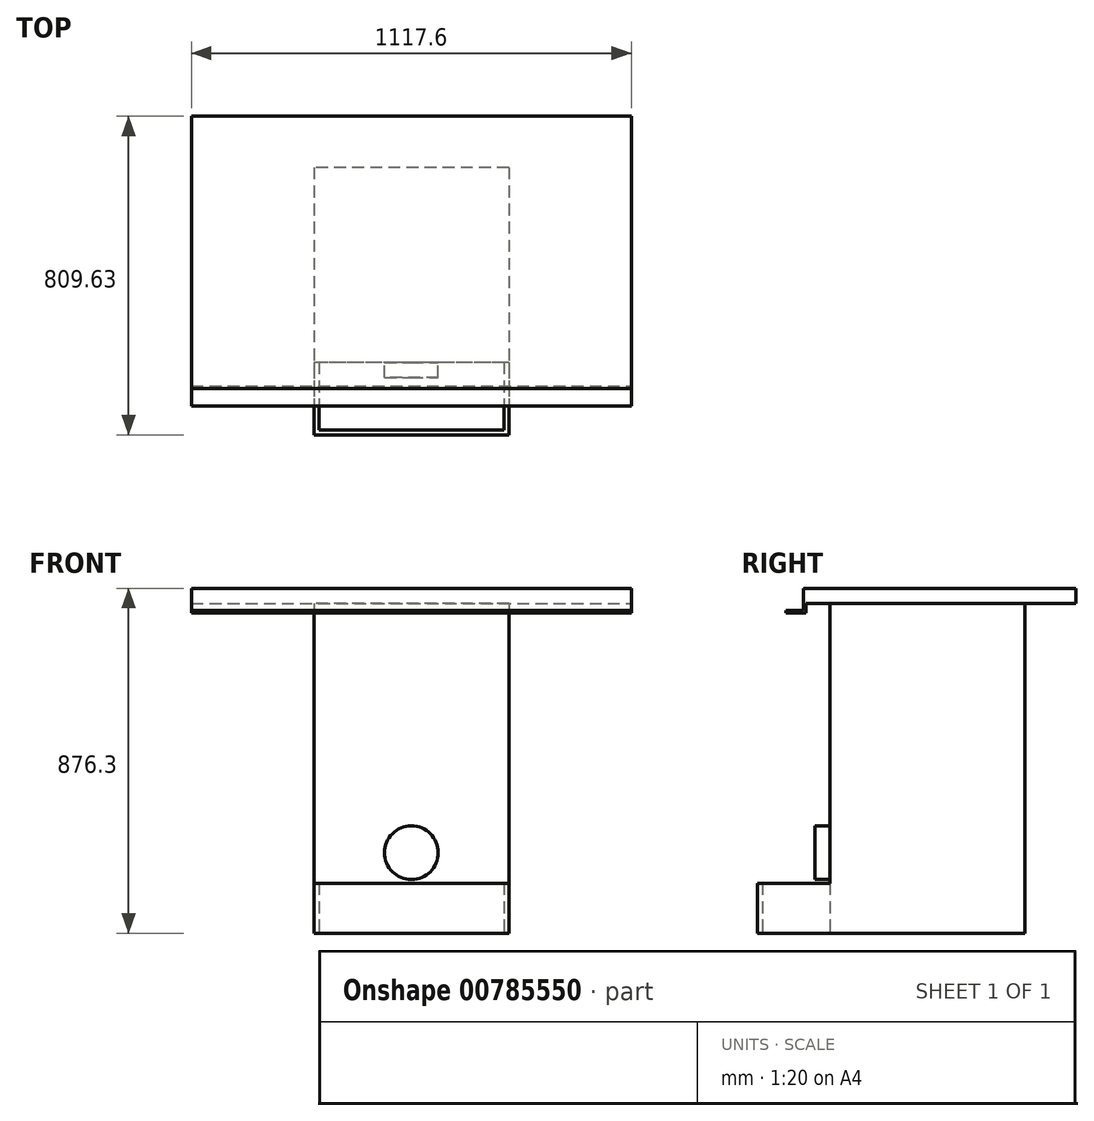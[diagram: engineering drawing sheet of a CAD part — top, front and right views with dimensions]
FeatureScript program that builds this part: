
annotation { "Feature Type Name" : "Feature", "Feature Type Description" : "" }
export const myFeature = defineFeature(function(context is Context, id is Id, definition is map)
    precondition{}
    {
        {
            var Q0;
            Q0=qCreatedBy(makeId("Top.planeOp"),FACE);
            var sketch = newSketch(context, id + "F0", { "sketchPlane" : qUnion([Q0])});
            skLineSegment(sketch, "E0.bottom", {"start": v(247.65, 247.65) * mm, "end": v(-247.65, 247.65) * mm});
            skLineSegment(sketch, "E0.top", {"start": v(247.65, -247.65) * mm, "end": v(-247.65, -247.65) * mm});
            skLineSegment(sketch, "E0.left", {"start": v(247.65, 247.65) * mm, "end": v(247.65, -247.65) * mm});
            skLineSegment(sketch, "E0.right", {"start": v(-247.65, 247.65) * mm, "end": v(-247.65, -247.65) * mm});
            skPoint(sketch, "E0.middle", {"position": v(0, 0) * mm});
            skSolve(sketch);
        }
        {
            var Q0;
            Q0 = qSketchRegion(id + "F0", true);
            extrude(context, id + "F1", {"entities" : qUnion([Q0]), "depth" : 838.2 * mm, "offsetDistance" : 25.4 * mm});
        }
        {
            var Q0;
            Q0=makeQuery(id+"F1.opExtrude","SWEPT_FACE",FACE,{"disambiguationData":[OSD([sQuery(id+"F0.wireOp",EDGE,"E0.top")])]});
            var sketch = newSketch(context, id + "F2", { "sketchPlane" : qUnion([Q0])});
            skLineSegment(sketch, "E1", {"start": v(0, 0) * mm, "end": v(0, 273.05) * mm});
            skCircle(sketch, "E2", {"center": v(0, 204.79) * mm, "radius": 68.26 * mm});
            skSolve(sketch);
        }
        {
            var Q0;
            {var subQ0=sQuery(id+"F2.wireOp",EDGE,"E2");var subQ1=sQuery(id+"F2.wireOp",EDGE,"E1");var subQ2=makeQuery(id+"F2.imprint","INTERSECT",VERTEX,{"disambiguationData":[OD(0.0)],"derivedFrom":[subQ1,subQ0]});Q0=makeQuery(id+"F2.imprint","IMPRINT",FACE,{"disambiguationData":[TD([[makeQuery(id+"F2.imprint","IMPRINT",EDGE,{"disambiguationData":[TD([[subQ2,1.0]])],"derivedFrom":subQ1}),1.0]])]});}
            var Q1;
            {var subQ0=sQuery(id+"F2.wireOp",EDGE,"E2");var subQ1=sQuery(id+"F2.wireOp",EDGE,"E1");var subQ2=makeQuery(id+"F2.imprint","INTERSECT",VERTEX,{"disambiguationData":[OD(0.0)],"derivedFrom":[subQ1,subQ0]});Q1=makeQuery(id+"F2.imprint","IMPRINT",FACE,{"disambiguationData":[TD([[makeQuery(id+"F2.imprint","IMPRINT",EDGE,{"disambiguationData":[TD([[subQ2,1.0]])],"derivedFrom":subQ1}),-1.0]])]});}
            extrude(context, id + "F3", {"entities" : qUnion([Q0, Q1]), "operationType" : NewBodyOperationType.ADD, "depth" : 38.1 * mm, "offsetDistance" : 25.4 * mm});
        }
        {
            var Q0;
            Q0=makeQuery(id+"F1.opExtrude","CAP_FACE",FACE,{"disambiguationData":[OSD([sQuery(id+"F0.wireOp",EDGE,"E0.bottom"),sQuery(id+"F0.wireOp",EDGE,"E0.top"),sQuery(id+"F0.wireOp",EDGE,"E0.left"),sQuery(id+"F0.wireOp",EDGE,"E0.right")])],"isStart":false});
            var sketch = newSketch(context, id + "F4", { "sketchPlane" : qUnion([Q0])});
            skLineSegment(sketch, "E3", {"start": v(-247.65, -247.65) * mm, "end": v(-558.8, -247.65) * mm});
            skLineSegment(sketch, "E4", {"start": v(247.65, -247.65) * mm, "end": v(558.8, -247.65) * mm});
            skLineSegment(sketch, "E5", {"start": v(-558.8, -247.65) * mm, "end": v(-558.8, -307.98) * mm});
            skLineSegment(sketch, "E6.bottom", {"start": v(-558.8, -307.98) * mm, "end": v(558.8, -307.98) * mm});
            skLineSegment(sketch, "E6.top", {"start": v(-558.8, 377.83) * mm, "end": v(558.8, 377.83) * mm});
            skLineSegment(sketch, "E6.left", {"start": v(-558.8, -307.98) * mm, "end": v(-558.8, 377.83) * mm});
            skLineSegment(sketch, "E6.right", {"start": v(558.8, -307.98) * mm, "end": v(558.8, 377.83) * mm});
            skSolve(sketch);
        }
        {
            var Q0;
            Q0 = qSketchRegion(id + "F4", true);
            extrude(context, id + "F5", {"entities" : qUnion([Q0]), "operationType" : NewBodyOperationType.ADD, "depth" : 38.1 * mm, "offsetDistance" : 25.4 * mm});
        }
        {
            var Q0;
            Q0=makeQuery(id+"F5.opExtrude","SWEPT_FACE",FACE,{"disambiguationData":[OSD([sQuery(id+"F4.wireOp",EDGE,"E6.right")])]});
            var sketch = newSketch(context, id + "F6", { "sketchPlane" : qUnion([Q0])});
            skLineSegment(sketch, "E7", {"start": v(-307.98, 876.3) * mm, "end": v(-314.33, 876.3) * mm});
            skLineSegment(sketch, "E8", {"start": v(-314.33, 876.3) * mm, "end": v(-314.33, 820.74) * mm});
            skLineSegment(sketch, "E9", {"start": v(-314.33, 820.74) * mm, "end": v(-358.78, 820.74) * mm});
            skLineSegment(sketch, "E10", {"start": v(-358.78, 820.74) * mm, "end": v(-358.78, 814.39) * mm});
            skLineSegment(sketch, "E11", {"start": v(-358.78, 814.39) * mm, "end": v(-307.98, 814.39) * mm});
            skLineSegment(sketch, "E12", {"start": v(-307.98, 814.39) * mm, "end": v(-307.98, 838.2) * mm});
            skLineSegment(sketch, "E13", {"start": v(-307.98, 838.2) * mm, "end": v(-307.98, 876.3) * mm});
            skSolve(sketch);
        }
        {
            var Q0;
            Q0 = qSketchRegion(id + "F6", true);
            extrude(context, id + "F7", {"entities" : qUnion([Q0]), "operationType" : NewBodyOperationType.ADD, "oppositeDirection" : true, "depth" : 1117.6 * mm, "offsetDistance" : 25.4 * mm});
        }
        {
            var Q0;
            Q0=makeQuery(id+"F1.opExtrude","CAP_FACE",FACE,{"disambiguationData":[OSD([sQuery(id+"F0.wireOp",EDGE,"E0.bottom"),sQuery(id+"F0.wireOp",EDGE,"E0.top"),sQuery(id+"F0.wireOp",EDGE,"E0.left"),sQuery(id+"F0.wireOp",EDGE,"E0.right")])],"isStart":true});
            var sketch = newSketch(context, id + "F8", { "sketchPlane" : qUnion([Q0])});
            skLineSegment(sketch, "E14", {"start": v(247.65, 247.65) * mm, "end": v(247.65, 431.8) * mm});
            skLineSegment(sketch, "E15", {"start": v(-247.65, 247.65) * mm, "end": v(-247.65, 431.8) * mm});
            skLineSegment(sketch, "E16", {"start": v(-247.65, 431.8) * mm, "end": v(247.65, 431.8) * mm});
            skLineSegment(sketch, "E17", {"start": v(247.65, 247.65) * mm, "end": v(234.95, 247.65) * mm});
            skLineSegment(sketch, "E18", {"start": v(234.95, 247.65) * mm, "end": v(234.95, 419.1) * mm});
            skLineSegment(sketch, "E19.MirrorCS", {"start": v(-234.95, 247.65) * mm, "end": v(-234.95, 419.1) * mm});
            skLineSegment(sketch, "E20", {"start": v(-234.95, 419.1) * mm, "end": v(234.95, 419.1) * mm});
            skSolve(sketch);
        }
        {
            var Q0;
            Q0 = qSketchRegion(id + "F8", true);
            var Q1;
            Q1=makeQuery(id+"F8.imprint","IMPRINT",FACE,{"disambiguationData":[TD([[makeQuery(id+"F8.imprint","IMPRINT",EDGE,{"derivedFrom":sQuery(id+"F8.wireOp",EDGE,"E14")}),1.0]])]});
            extrude(context, id + "F9", {"entities" : qUnion([Q0, Q1]), "operationType" : NewBodyOperationType.ADD, "oppositeDirection" : true, "depth" : 127 * mm, "offsetDistance" : 25.4 * mm});
        }
    });
